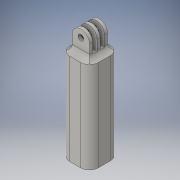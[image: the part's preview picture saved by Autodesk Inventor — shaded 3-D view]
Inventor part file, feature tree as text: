
AUTODESK INVENTOR PART (.ipt)
format: ipt  version: 2016 (Build 200138000, 138)  size: 198,656 bytes
history: native  units: in
note: dims shown in document units (in); Inventor stores cm internally (conversion verified against a paired STEP export)
features: extrude x4, sketch x4, fillet x3
ambient origin geometry x8: Origin, YZ Plane, XZ Plane, XY Plane, X Axis, Y Axis, Z Axis, Center Point
bodies: Solid1 (feature_tree)
feature tree (11):
  extrude  "Extrusion1"  Depth=0.2953in
  fillet  "Fillet1"  Radius=0.6496in
  extrude  "Extrusion8"  Depth=0.2559in
  extrude  "Extrusion9"  Depth=0.2953in
  extrude  "Extrusion10"  Depth=0.3in
  fillet  "Fillet2"  Radius=0.1063in
  fillet  "Fillet3"  Radius=0.626in
  sketch  "Sketch4"  dims[d0=0.2953in d1=0.2953in d2=0.6496in]
  sketch  "Sketch13"  dims[d3=0.1969in d4=0.2559in]
  sketch  "Sketch14"  dims[d5=0.626in d6=0.0in d7=0.2953in]
  sketch  "Sketch15"  dims[d47=0.1063in d48=0.1063in d49=0.1063in d50=0.626in d51=0.1535in d52=0.1535in d53=1.0in d54=0.0in d55=0.1575in d56=0.0in d57=0.1969in d58=0.1969in d59=0.1969in d60=0.1969in d61=3.1496in d62=0.0in d63=0.2in d64=0.3in]
